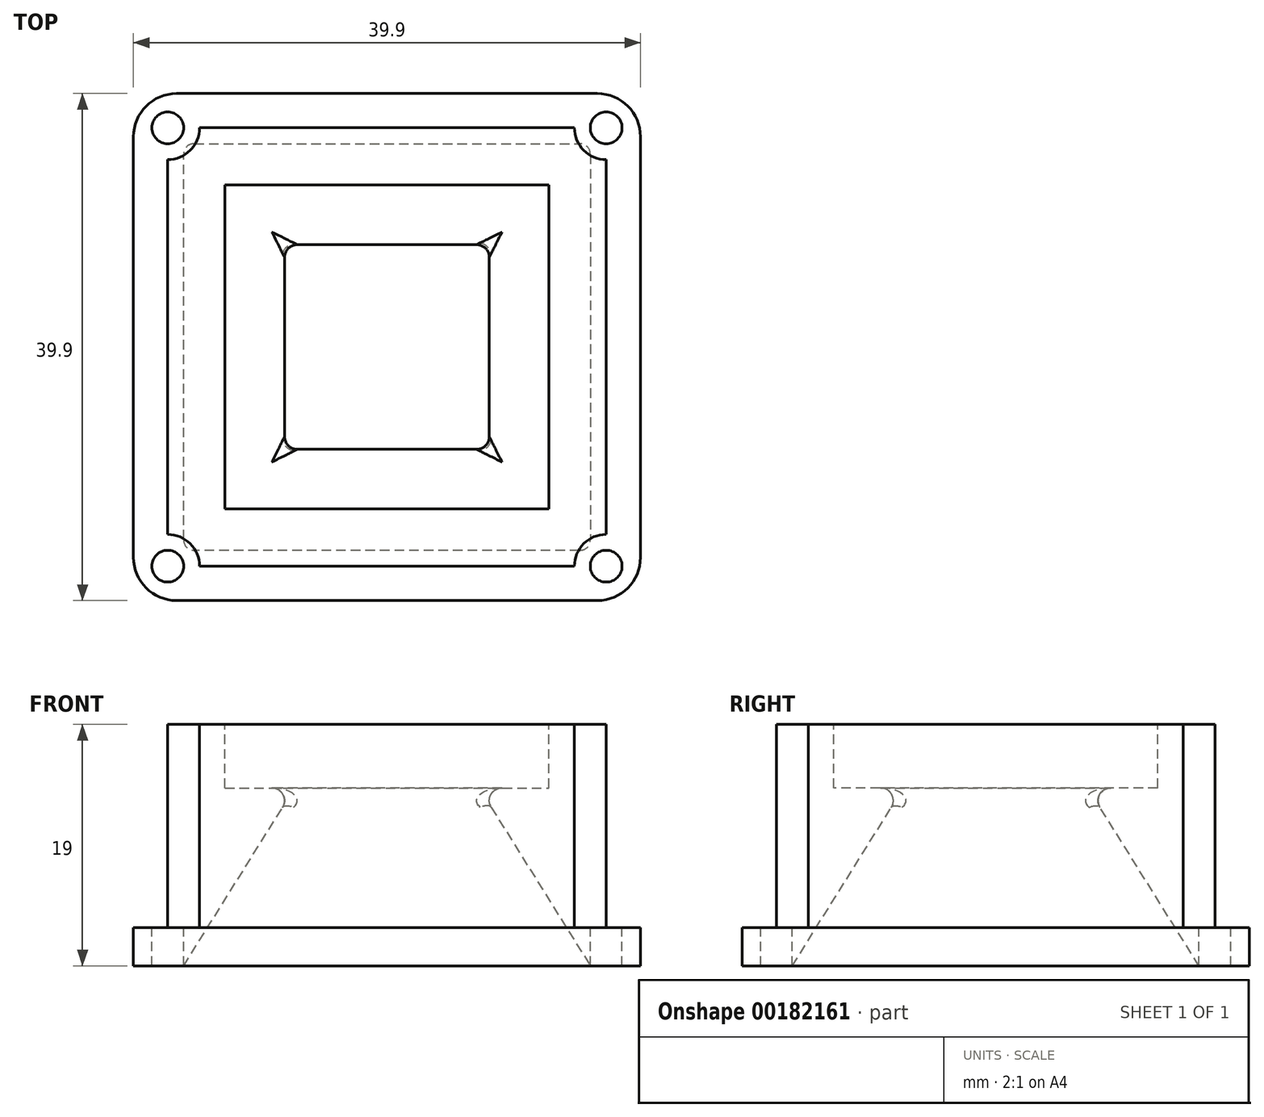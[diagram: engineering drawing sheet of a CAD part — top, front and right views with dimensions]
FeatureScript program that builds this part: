
annotation { "Feature Type Name" : "Feature", "Feature Type Description" : "" }
export const myFeature = defineFeature(function(context is Context, id is Id, definition is map)
    precondition{}
    {
        {
            var Q0;
            Q0=qCreatedBy(makeId("Top.planeOp"),FACE);
            var sketch = newSketch(context, id + "F0", { "sketchPlane" : qUnion([Q0])});
            skLineSegment(sketch, "E0.bottom", {"start": v(19.95, -19.95) * mm, "end": v(-19.95, -19.95) * mm});
            skLineSegment(sketch, "E0.top", {"start": v(19.95, 19.95) * mm, "end": v(-19.95, 19.95) * mm});
            skLineSegment(sketch, "E0.left", {"start": v(19.95, -19.95) * mm, "end": v(19.95, 19.95) * mm});
            skLineSegment(sketch, "E0.right", {"start": v(-19.95, -19.95) * mm, "end": v(-19.95, 19.95) * mm});
            skPoint(sketch, "E0.middle", {"position": v(0, 0) * mm});
            skSolve(sketch);
        }
        {
            var Q0;
            Q0 = qSketchRegion(id + "F0", true);
            extrude(context, id + "F1", {"entities" : qUnion([Q0]), "depth" : 3 * mm});
        }
        {
            var Q0;
            Q0=makeQuery(id+"F1.opExtrude","SWEPT_EDGE",EDGE,{"disambiguationData":[OSD([sQuery(id+"F0.wireOp",EDGE,"E0.bottom"),sQuery(id+"F0.wireOp",EDGE,"E0.right")])]});
            var Q1;
            Q1=makeQuery(id+"F1.opExtrude","SWEPT_EDGE",EDGE,{"disambiguationData":[OSD([sQuery(id+"F0.wireOp",EDGE,"E0.bottom"),sQuery(id+"F0.wireOp",EDGE,"E0.left")])]});
            var Q2;
            Q2=makeQuery(id+"F1.opExtrude","SWEPT_EDGE",EDGE,{"disambiguationData":[OSD([sQuery(id+"F0.wireOp",EDGE,"E0.top"),sQuery(id+"F0.wireOp",EDGE,"E0.left")])]});
            var Q3;
            Q3=makeQuery(id+"F1.opExtrude","SWEPT_EDGE",EDGE,{"disambiguationData":[OSD([sQuery(id+"F0.wireOp",EDGE,"E0.top"),sQuery(id+"F0.wireOp",EDGE,"E0.right")])]});
            fillet(context, id + "F2", {"entities" : qUnion([Q0, Q1, Q2, Q3]), "radius" : 3.4 * mm, "tangentPropagation" : true, "allowEdgeOverflow" : false});
        }
        {
            var Q0;
            Q0=makeQuery(id+"F1.opExtrude","CAP_FACE",FACE,{"disambiguationData":[OSD([sQuery(id+"F0.wireOp",EDGE,"E0.bottom"),sQuery(id+"F0.wireOp",EDGE,"E0.top"),sQuery(id+"F0.wireOp",EDGE,"E0.left"),sQuery(id+"F0.wireOp",EDGE,"E0.right")])],"isStart":false});
            var sketch = newSketch(context, id + "F3", { "sketchPlane" : qUnion([Q0])});
            skLineSegment(sketch, "E1.bottom", {"start": v(-17.25, 17.25) * mm, "end": v(17.25, 17.25) * mm});
            skLineSegment(sketch, "E1.top", {"start": v(-17.25, -17.25) * mm, "end": v(17.25, -17.25) * mm});
            skLineSegment(sketch, "E1.left", {"start": v(-17.25, 17.25) * mm, "end": v(-17.25, -17.25) * mm});
            skLineSegment(sketch, "E1.right", {"start": v(17.25, 17.25) * mm, "end": v(17.25, -17.25) * mm});
            skPoint(sketch, "E1.middle", {"position": v(0, 0) * mm});
            skSolve(sketch);
        }
        {
            var Q0;
            Q0 = qSketchRegion(id + "F3", true);
            extrude(context, id + "F4", {"entities" : qUnion([Q0]), "operationType" : NewBodyOperationType.ADD, "depth" : 16 * mm});
        }
        {
            var Q0;
            Q0=makeQuery(id+"F4.opExtrude","CAP_FACE",FACE,{"disambiguationData":[OSD([sQuery(id+"F3.wireOp",EDGE,"E1.bottom"),sQuery(id+"F3.wireOp",EDGE,"E1.top"),sQuery(id+"F3.wireOp",EDGE,"E1.left"),sQuery(id+"F3.wireOp",EDGE,"E1.right")])],"isStart":false});
            var sketch = newSketch(context, id + "F5", { "sketchPlane" : qUnion([Q0])});
            skLineSegment(sketch, "E2.bottom", {"start": v(-12.75, 12.75) * mm, "end": v(12.75, 12.75) * mm});
            skLineSegment(sketch, "E2.top", {"start": v(-12.75, -12.75) * mm, "end": v(12.75, -12.75) * mm});
            skLineSegment(sketch, "E2.left", {"start": v(-12.75, 12.75) * mm, "end": v(-12.75, -12.75) * mm});
            skLineSegment(sketch, "E2.right", {"start": v(12.75, 12.75) * mm, "end": v(12.75, -12.75) * mm});
            skPoint(sketch, "E2.middle", {"position": v(0, 0) * mm});
            skSolve(sketch);
        }
        {
            var Q0;
            Q0 = qSketchRegion(id + "F5", true);
            extrude(context, id + "F6", {"entities" : qUnion([Q0]), "operationType" : NewBodyOperationType.REMOVE, "oppositeDirection" : true, "depth" : 5 * mm});
        }
        {
            var Q0;
            Q0=makeQuery(id+"F1.opExtrude","CAP_FACE",FACE,{"disambiguationData":[OSD([sQuery(id+"F0.wireOp",EDGE,"E0.bottom"),sQuery(id+"F0.wireOp",EDGE,"E0.top"),sQuery(id+"F0.wireOp",EDGE,"E0.left"),sQuery(id+"F0.wireOp",EDGE,"E0.right")])],"isStart":true});
            var sketch = newSketch(context, id + "F7", { "sketchPlane" : qUnion([Q0])});
            skLineSegment(sketch, "E3.bottom", {"start": v(16, -16) * mm, "end": v(-16, -16) * mm});
            skLineSegment(sketch, "E3.top", {"start": v(16, 16) * mm, "end": v(-16, 16) * mm});
            skLineSegment(sketch, "E3.left", {"start": v(16, -16) * mm, "end": v(16, 16) * mm});
            skLineSegment(sketch, "E3.right", {"start": v(-16, -16) * mm, "end": v(-16, 16) * mm});
            skPoint(sketch, "E3.middle", {"position": v(0, 0) * mm});
            skSolve(sketch);
        }
        {
            var Q0;
            Q0 = qSketchRegion(id + "F7", true);
            extrude(context, id + "F8", {"entities" : qUnion([Q0]), "operationType" : NewBodyOperationType.REMOVE, "oppositeDirection" : true, "depth" : 25 * mm, "hasDraft" : true, "draftAngle" : 32 * degree, "draftPullDirection" : true});
        }
        {
            var Q0;
            Q0=makeQuery(id+"F8.boolean.opBoolean","INTERSECT",EDGE,{"derivedFrom":[makeQuery(id+"F6.boolean.opBoolean","COPY",FACE,{"derivedFrom":makeQuery(id+"F6.opExtrude","CAP_FACE",FACE,{"disambiguationData":[OSD([sQuery(id+"F5.wireOp",EDGE,"E2.bottom"),sQuery(id+"F5.wireOp",EDGE,"E2.top"),sQuery(id+"F5.wireOp",EDGE,"E2.left"),sQuery(id+"F5.wireOp",EDGE,"E2.right")])],"isStart":false})}),makeQuery(id+"F8.opExtrude","SWEPT_FACE",FACE,{"disambiguationData":[OSD([sQuery(id+"F7.wireOp",EDGE,"E3.bottom")])]})]});
            var Q1;
            Q1=makeQuery(id+"F8.boolean.opBoolean","INTERSECT",EDGE,{"derivedFrom":[makeQuery(id+"F6.boolean.opBoolean","COPY",FACE,{"derivedFrom":makeQuery(id+"F6.opExtrude","CAP_FACE",FACE,{"disambiguationData":[OSD([sQuery(id+"F5.wireOp",EDGE,"E2.bottom"),sQuery(id+"F5.wireOp",EDGE,"E2.top"),sQuery(id+"F5.wireOp",EDGE,"E2.left"),sQuery(id+"F5.wireOp",EDGE,"E2.right")])],"isStart":false})}),makeQuery(id+"F8.opExtrude","SWEPT_FACE",FACE,{"disambiguationData":[OSD([sQuery(id+"F7.wireOp",EDGE,"E3.right")])]})]});
            var Q2;
            Q2=makeQuery(id+"F8.boolean.opBoolean","INTERSECT",EDGE,{"derivedFrom":[makeQuery(id+"F6.boolean.opBoolean","COPY",FACE,{"derivedFrom":makeQuery(id+"F6.opExtrude","CAP_FACE",FACE,{"disambiguationData":[OSD([sQuery(id+"F5.wireOp",EDGE,"E2.bottom"),sQuery(id+"F5.wireOp",EDGE,"E2.top"),sQuery(id+"F5.wireOp",EDGE,"E2.left"),sQuery(id+"F5.wireOp",EDGE,"E2.right")])],"isStart":false})}),makeQuery(id+"F8.opExtrude","SWEPT_FACE",FACE,{"disambiguationData":[OSD([sQuery(id+"F7.wireOp",EDGE,"E3.top")])]})]});
            var Q3;
            Q3=makeQuery(id+"F8.boolean.opBoolean","INTERSECT",EDGE,{"derivedFrom":[makeQuery(id+"F6.boolean.opBoolean","COPY",FACE,{"derivedFrom":makeQuery(id+"F6.opExtrude","CAP_FACE",FACE,{"disambiguationData":[OSD([sQuery(id+"F5.wireOp",EDGE,"E2.bottom"),sQuery(id+"F5.wireOp",EDGE,"E2.top"),sQuery(id+"F5.wireOp",EDGE,"E2.left"),sQuery(id+"F5.wireOp",EDGE,"E2.right")])],"isStart":false})}),makeQuery(id+"F8.opExtrude","SWEPT_FACE",FACE,{"disambiguationData":[OSD([sQuery(id+"F7.wireOp",EDGE,"E3.left")])]})]});
            fillet(context, id + "F9", {"entities" : qUnion([Q0, Q1, Q2, Q3]), "radius" : 1 * mm, "tangentPropagation" : true, "allowEdgeOverflow" : false});
        }
        {
            var Q0;
            Q0=makeQuery(id+"F8.boolean.opBoolean","COPY",EDGE,{"derivedFrom":makeQuery(id+"F8.opExtrude","SWEPT_EDGE",EDGE,{"disambiguationData":[OSD([sQuery(id+"F7.wireOp",EDGE,"E3.bottom"),sQuery(id+"F7.wireOp",EDGE,"E3.left")])]})});
            var Q1;
            Q1=makeQuery(id+"F8.boolean.opBoolean","COPY",EDGE,{"derivedFrom":makeQuery(id+"F8.opExtrude","SWEPT_EDGE",EDGE,{"disambiguationData":[OSD([sQuery(id+"F7.wireOp",EDGE,"E3.top"),sQuery(id+"F7.wireOp",EDGE,"E3.left")])]})});
            var Q2;
            Q2=makeQuery(id+"F8.boolean.opBoolean","COPY",EDGE,{"derivedFrom":makeQuery(id+"F8.opExtrude","SWEPT_EDGE",EDGE,{"disambiguationData":[OSD([sQuery(id+"F7.wireOp",EDGE,"E3.top"),sQuery(id+"F7.wireOp",EDGE,"E3.right")])]})});
            var Q3;
            Q3=makeQuery(id+"F8.boolean.opBoolean","COPY",EDGE,{"derivedFrom":makeQuery(id+"F8.opExtrude","SWEPT_EDGE",EDGE,{"disambiguationData":[OSD([sQuery(id+"F7.wireOp",EDGE,"E3.bottom"),sQuery(id+"F7.wireOp",EDGE,"E3.right")])]})});
            fillet(context, id + "F10", {"entities" : qUnion([Q0, Q1, Q2, Q3]), "radius" : 1 * mm, "tangentPropagation" : true, "allowEdgeOverflow" : false});
        }
        {
            var Q0;
            Q0=makeQuery(id+"F4.opExtrude","CAP_FACE",FACE,{"disambiguationData":[OSD([sQuery(id+"F3.wireOp",EDGE,"E1.bottom"),sQuery(id+"F3.wireOp",EDGE,"E1.top"),sQuery(id+"F3.wireOp",EDGE,"E1.left"),sQuery(id+"F3.wireOp",EDGE,"E1.right")])],"isStart":false});
            var sketch = newSketch(context, id + "F11", { "sketchPlane" : qUnion([Q0])});
            skCircle(sketch, "E4", {"center": v(-17.25, -17.25) * mm, "radius": 2.5 * mm});
            skCircle(sketch, "E5", {"center": v(17.25, -17.25) * mm, "radius": 2.5 * mm});
            skCircle(sketch, "E6", {"center": v(17.25, 17.25) * mm, "radius": 2.5 * mm});
            skCircle(sketch, "E7", {"center": v(-17.25, 17.25) * mm, "radius": 2.5 * mm});
            skSolve(sketch);
        }
        {
            var Q0;
            Q0 = qSketchRegion(id + "F11", true);
            var Q1;
            Q1=makeQuery(id+"F1.opExtrude","CAP_FACE",FACE,{"disambiguationData":[OSD([sQuery(id+"F0.wireOp",EDGE,"E0.bottom"),sQuery(id+"F0.wireOp",EDGE,"E0.top"),sQuery(id+"F0.wireOp",EDGE,"E0.left"),sQuery(id+"F0.wireOp",EDGE,"E0.right")])],"isStart":false});
            extrude(context, id + "F12", {"entities" : qUnion([Q0]), "operationType" : NewBodyOperationType.REMOVE, "endBound" : BoundingType.UP_TO_SURFACE, "oppositeDirection" : true, "endBoundEntityFace" : qUnion([Q1]), "depth" : 25 * mm});
        }
        {
            var Q0;
            Q0=makeQuery(id+"F12.boolean.opBoolean","MERGE",FACE,{"derivedFrom":[makeQuery(id+"F1.opExtrude","CAP_FACE",FACE,{"disambiguationData":[OSD([sQuery(id+"F0.wireOp",EDGE,"E0.bottom"),sQuery(id+"F0.wireOp",EDGE,"E0.top"),sQuery(id+"F0.wireOp",EDGE,"E0.left"),sQuery(id+"F0.wireOp",EDGE,"E0.right")])],"isStart":false})],"fromTools":[makeQuery(id+"F12.opExtrude","CAP_FACE",FACE,{"disambiguationData":[OSD([sQuery(id+"F11.wireOp",EDGE,"E4")])],"isStart":false}),makeQuery(id+"F12.opExtrude","CAP_FACE",FACE,{"disambiguationData":[OSD([sQuery(id+"F11.wireOp",EDGE,"E5")])],"isStart":false}),makeQuery(id+"F12.opExtrude","CAP_FACE",FACE,{"disambiguationData":[OSD([sQuery(id+"F11.wireOp",EDGE,"E6")])],"isStart":false}),makeQuery(id+"F12.opExtrude","CAP_FACE",FACE,{"disambiguationData":[OSD([sQuery(id+"F11.wireOp",EDGE,"E7")])],"isStart":false})]});
            var sketch = newSketch(context, id + "F13", { "sketchPlane" : qUnion([Q0])});
            skCircle(sketch, "E8", {"center": v(-17.25, -17.25) * mm, "radius": 1.25 * mm});
            skCircle(sketch, "E9", {"center": v(17.25, -17.25) * mm, "radius": 1.25 * mm});
            skCircle(sketch, "E10", {"center": v(17.25, 17.25) * mm, "radius": 1.25 * mm});
            skCircle(sketch, "E11", {"center": v(-17.25, 17.25) * mm, "radius": 1.25 * mm});
            skSolve(sketch);
        }
        {
            var Q0;
            Q0 = qSketchRegion(id + "F13", true);
            extrude(context, id + "F14", {"entities" : qUnion([Q0]), "operationType" : NewBodyOperationType.REMOVE, "oppositeDirection" : true, "depth" : 25 * mm});
        }
    });
